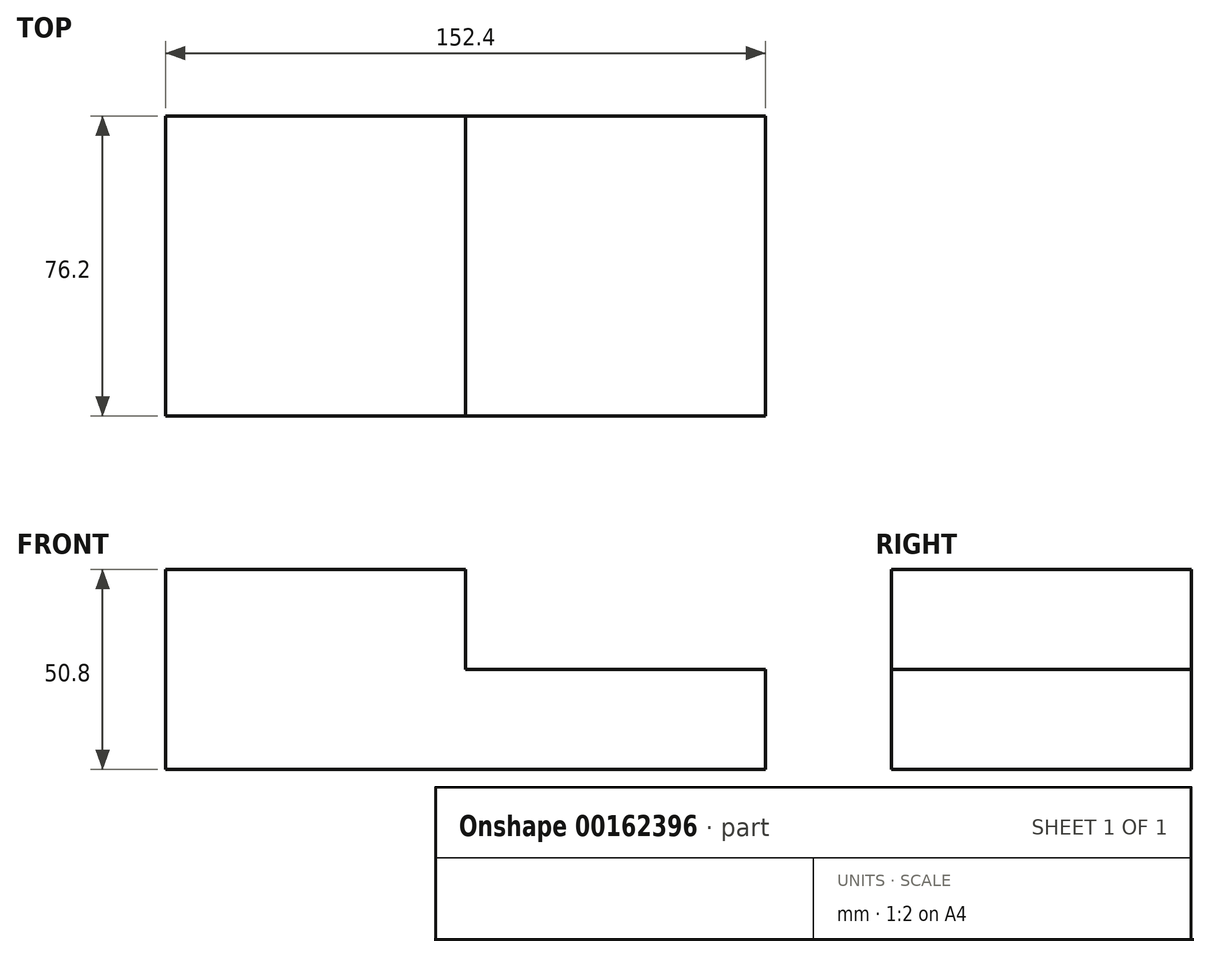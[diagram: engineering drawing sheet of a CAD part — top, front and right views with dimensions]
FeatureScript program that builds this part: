
annotation { "Feature Type Name" : "Feature", "Feature Type Description" : "" }
export const myFeature = defineFeature(function(context is Context, id is Id, definition is map)
    precondition{}
    {
        {
            var Q0;
            Q0=qCreatedBy(makeId("Front.planeOp"),FACE);
            var sketch = newSketch(context, id + "F0", { "sketchPlane" : qUnion([Q0])});
            skLineSegment(sketch, "E0", {"start": v(0, 50.8) * mm, "end": v(0, 0) * mm});
            skLineSegment(sketch, "E1", {"start": v(0, 0) * mm, "end": v(152.4, 0) * mm});
            skLineSegment(sketch, "E2", {"start": v(152.4, 0) * mm, "end": v(152.4, 25.4) * mm});
            skLineSegment(sketch, "E3", {"start": v(152.4, 25.4) * mm, "end": v(76.2, 25.4) * mm});
            skLineSegment(sketch, "E4", {"start": v(76.2, 25.4) * mm, "end": v(76.2, 50.8) * mm});
            skLineSegment(sketch, "E5", {"start": v(76.2, 50.8) * mm, "end": v(0, 50.8) * mm});
            skSolve(sketch);
        }
        {
            var Q0;
            Q0 = qSketchRegion(id + "F0", true);
            extrude(context, id + "F1", {"entities" : qUnion([Q0]), "depth" : 76.2 * mm});
        }
    });
